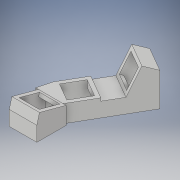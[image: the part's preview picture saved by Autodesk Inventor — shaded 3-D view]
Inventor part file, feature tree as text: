
AUTODESK INVENTOR PART (.ipt)
format: ipt  version: 2017 (Build 210142000, 142)  size: 184,832 bytes
history: native  units: in
note: dims shown in document units (in); Inventor stores cm internally (conversion verified against a paired STEP export)
features: extrude x6, sketch x6, shell x1
ambient origin geometry x8: Origin, YZ Plane, XZ Plane, XY Plane, X Axis, Y Axis, Z Axis, Center Point
bodies: Solid1 (feature_tree)
feature tree (13):
  extrude  "Extrusion1"  Depth=0.748in
  extrude  "Extrusion2"  Depth=0.4724in
  extrude  "Extrusion4"  Depth=0.748in
  shell  "Shell1"  Thickness=0.748in
  sketch  "Sketch4"  dims[d11=0.4724in d12=0.0in d16=0.748in]
  sketch  "Sketch5"  dims[d17=0.3937in d18=0.5512in]
  sketch  "Sketch6"  dims[d20=0.1718in d23=0.748in d25=30.0deg d26=0.748in d27=0.0787in d28=0.748in d29=0.0in d30=0.3937in d31=0.0984in d32=0.5512in d33=0.5512in d34=0.5512in d35=0.0984in d36=0.0984in d37=0.0625in d38=0.0in d39=0.748in d40=0.0in d41=0.0in d42=0.0in]
  extrude  "Extrusion5"  Depth=0.748in
  extrude  "Extrusion6"  Depth=0.5512in
  extrude  "Extrusion7"  Depth=0.748in
  sketch  "Sketch1"  dims[d0=0.748in d1=0.2756in]
  sketch  "Sketch2"  dims[d2=105.0deg d3=0.4724in]
  sketch  "Sketch3"  dims[d4=0.748in d5=0.0in d6=0.748in d10=0.748in]
